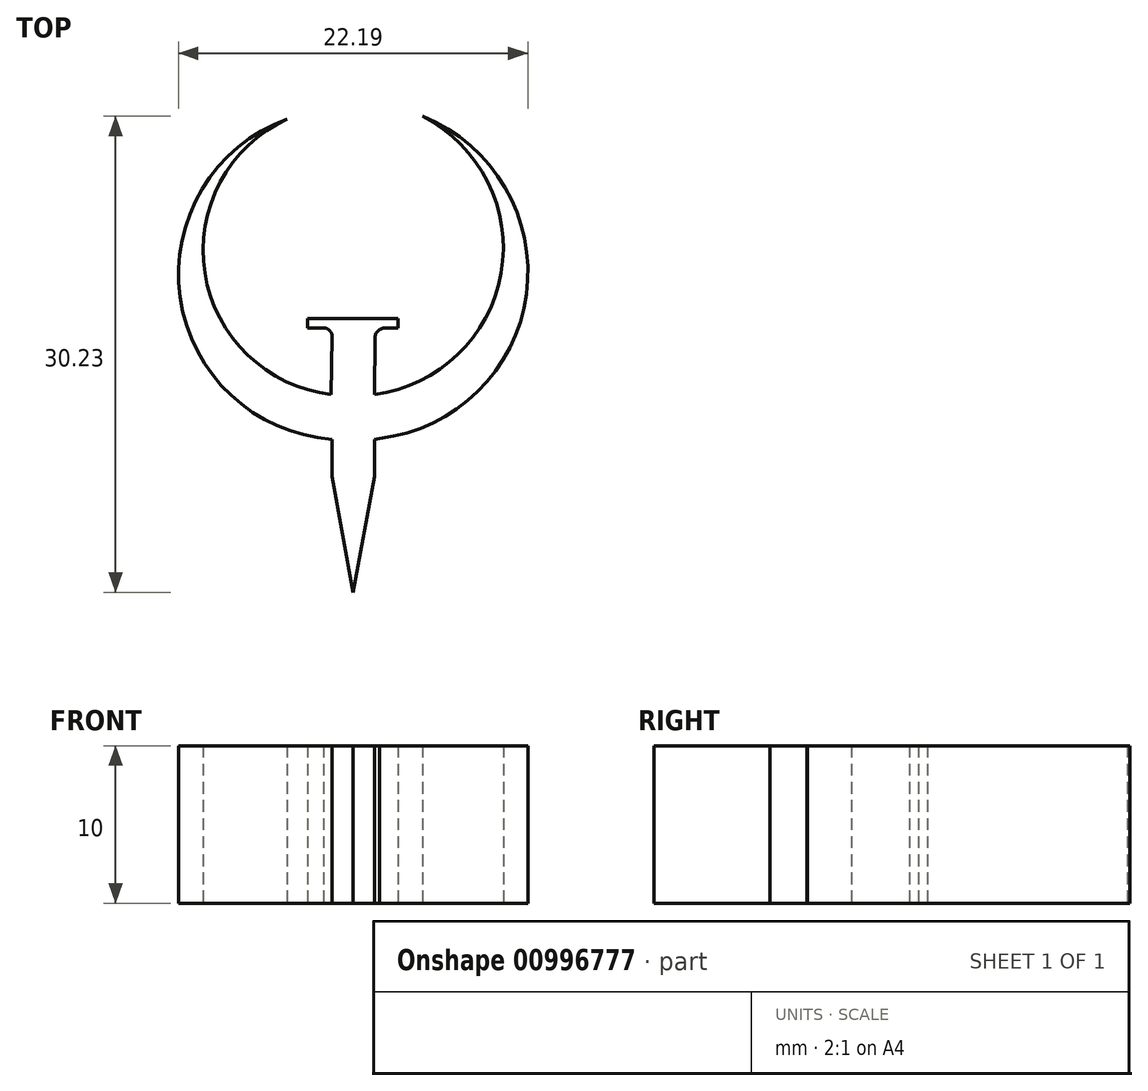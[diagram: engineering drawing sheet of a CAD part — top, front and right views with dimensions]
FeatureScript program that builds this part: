
annotation { "Feature Type Name" : "Feature", "Feature Type Description" : "" }
export const myFeature = defineFeature(function(context is Context, id is Id, definition is map)
    precondition{}
    {
        {
            var Q0;
            Q0=qCreatedBy(makeId("Top.planeOp"),FACE);
            var sketch = newSketch(context, id + "F0", { "sketchPlane" : qUnion([Q0])});
            skArc(sketch, "E0", {"start": v(-14.86, 17.5) * mm, "mid": v(-20.1, 7.7) * mm, "end": v(-12.06, 0) * mm});
            skArc(sketch, "E1", {"start": v(-9.33, 0) * mm, "mid": v(-1.28, 7.7) * mm, "end": v(-6.27, 17.66) * mm});
            skArc(sketch, "E2", {"start": v(-9, -2.8) * mm, "mid": v(0.33, 6.36) * mm, "end": v(-6.27, 17.66) * mm});
            skArc(sketch, "E3", {"start": v(-14.86, 17.5) * mm, "mid": v(-21.67, 6.17) * mm, "end": v(-12.01, -2.85) * mm});
            skLineSegment(sketch, "E4", {"start": v(-13.57, 4.8) * mm, "end": v(-7.8, 4.8) * mm});
            skLineSegment(sketch, "E5", {"start": v(-7.8, 4.8) * mm, "end": v(-7.8, 4.23) * mm});
            skLineSegment(sketch, "E6", {"start": v(-7.8, 4.23) * mm, "end": v(-7.8, 4.8) * mm});
            skLineSegment(sketch, "E7", {"start": v(-13.57, 4.23) * mm, "end": v(-13.57, 4.8) * mm});
            skLineSegment(sketch, "E8", {"start": v(-13.57, 4.23) * mm, "end": v(-12.68, 4.23) * mm});
            skLineSegment(sketch, "E9", {"start": v(-12, 3.65) * mm, "end": v(-12.06, 0) * mm});
            skLineSegment(sketch, "E10", {"start": v(-9.3, 3.65) * mm, "end": v(-9.33, 0) * mm});
            skLineSegment(sketch, "E11", {"start": v(-7.8, 4.23) * mm, "end": v(-8.6, 4.23) * mm});
            skArc(sketch, "E12", {"start": v(-8.6, 4.23) * mm, "mid": v(-9.06, 4.06) * mm, "end": v(-9.3, 3.65) * mm});
            skArc(sketch, "E13", {"start": v(-12, 3.65) * mm, "mid": v(-12.17, 4.06) * mm, "end": v(-12.57, 4.23) * mm});
            skLineSegment(sketch, "E14", {"start": v(-12.01, -2.85) * mm, "end": v(-12.01, -5.2) * mm});
            skLineSegment(sketch, "E15", {"start": v(-12.01, -5.2) * mm, "end": v(-10.67, -12.57) * mm});
            skLineSegment(sketch, "E16", {"start": v(-10.67, -12.57) * mm, "end": v(-9.3, -5.2) * mm});
            skLineSegment(sketch, "E17", {"start": v(-9.3, -5.2) * mm, "end": v(-9.3, -2.85) * mm});
            skLineSegment(sketch, "E18", {"start": v(-9.3, -2.85) * mm, "end": v(-9, -2.8) * mm});
            skLineSegment(sketch, "E19", {"start": v(-12.57, 4.23) * mm, "end": v(-12.68, 4.23) * mm});
            skSolve(sketch);
        }
        {
            var Q0;
            Q0 = qSketchRegion(id + "F0", true);
            extrude(context, id + "F1", {"entities" : qUnion([Q0]), "depth" : 10 * mm, "offsetDistance" : 25 * mm});
        }
    });
